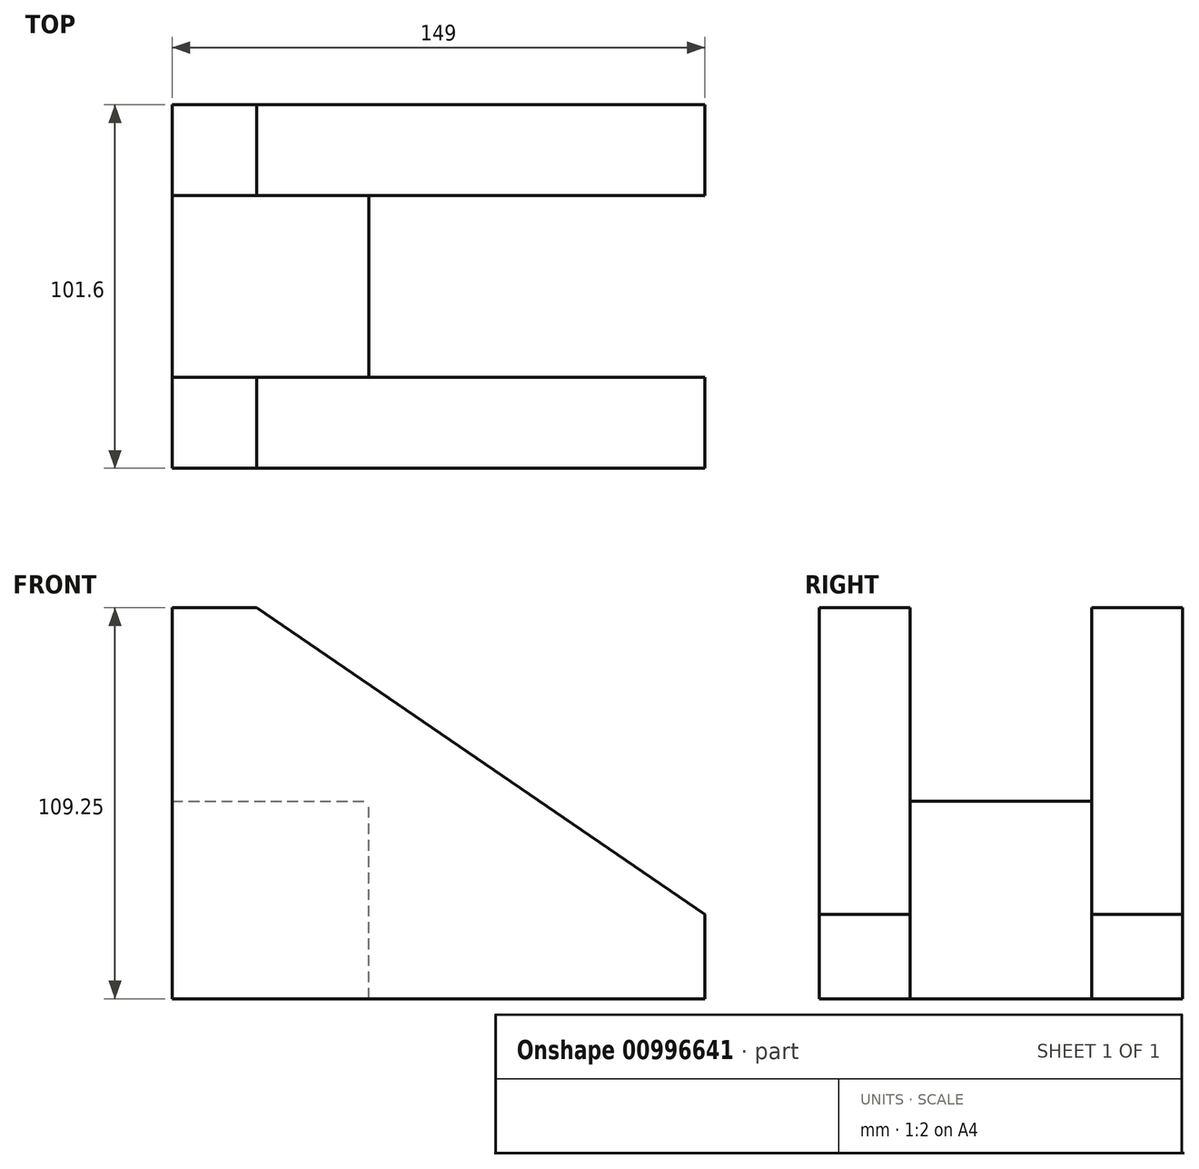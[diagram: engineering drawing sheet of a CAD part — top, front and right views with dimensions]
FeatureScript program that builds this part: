
annotation { "Feature Type Name" : "Feature", "Feature Type Description" : "" }
export const myFeature = defineFeature(function(context is Context, id is Id, definition is map)
    precondition{}
    {
        {
            var Q0;
            Q0=qCreatedBy(makeId("Front.planeOp"),FACE);
            var sketch = newSketch(context, id + "F0", { "sketchPlane" : qUnion([Q0])});
            skLineSegment(sketch, "E0", {"start": v(-68.4, -55.17) * mm, "end": v(80.59, -55.17) * mm});
            skLineSegment(sketch, "E1", {"start": v(80.59, -55.17) * mm, "end": v(80.59, -31.64) * mm});
            skLineSegment(sketch, "E2", {"start": v(80.59, -31.64) * mm, "end": v(-44.81, 54.08) * mm});
            skLineSegment(sketch, "E3", {"start": v(-44.81, 54.08) * mm, "end": v(-68.4, 54.08) * mm});
            skLineSegment(sketch, "E4", {"start": v(-68.4, 54.08) * mm, "end": v(-68.4, -55.17) * mm});
            skSolve(sketch);
        }
        {
            var Q0;
            Q0=makeQuery(id+"F0.imprint","IMPRINT",FACE,{"disambiguationData":[TD([[makeQuery(id+"F0.imprint","IMPRINT",EDGE,{"derivedFrom":sQuery(id+"F0.wireOp",EDGE,"E0")}),1.0]])]});
            extrude(context, id + "F1", {"entities" : qUnion([Q0]), "depth" : 25.4 * mm, "offsetDistance" : 25.4 * mm});
        }
        {
            var Q0;
            Q0=qCreatedBy(makeId("Front.planeOp"),FACE);
            cPlane(context, id + "F2", {"entities" : qUnion([Q0]), "cplaneType" : CPlaneType.OFFSET, "offset" : 25.4 * mm, "oppositeDirection" : true, "width" : 152.4 * mm, "height" : 152.4 * mm});
        }
        {
            var Q0;
            Q0=makeQuery(id+"F1.opExtrude","SWEPT_BODY",BODY,{"disambiguationData":[OSD([sQuery(id+"F0.wireOp",EDGE,"E0"),sQuery(id+"F0.wireOp",EDGE,"E1"),sQuery(id+"F0.wireOp",EDGE,"E2"),sQuery(id+"F0.wireOp",EDGE,"E3"),sQuery(id+"F0.wireOp",EDGE,"E4")])]});
            var Q1;
            Q1=qCreatedBy(id+"F2.planeOp",FACE);
            mirror(context, id + "F3", {"entities" : qUnion([Q0]), "mirrorPlane" : qUnion([Q1])});
        }
        {
            var Q0;
            Q0=makeQuery(id+"F1.opExtrude","CAP_FACE",FACE,{"disambiguationData":[OSD([sQuery(id+"F0.wireOp",EDGE,"E0"),sQuery(id+"F0.wireOp",EDGE,"E1"),sQuery(id+"F0.wireOp",EDGE,"E2"),sQuery(id+"F0.wireOp",EDGE,"E3"),sQuery(id+"F0.wireOp",EDGE,"E4")])],"isStart":true});
            var sketch = newSketch(context, id + "F4", { "sketchPlane" : qUnion([Q0])});
            skLineSegment(sketch, "E5.bottom", {"start": v(68.4, -55.17) * mm, "end": v(13.39, -55.17) * mm});
            skLineSegment(sketch, "E5.top", {"start": v(68.4, 0) * mm, "end": v(13.39, 0) * mm});
            skLineSegment(sketch, "E5.left", {"start": v(68.4, -55.17) * mm, "end": v(68.4, 0) * mm});
            skLineSegment(sketch, "E5.right", {"start": v(13.39, -55.17) * mm, "end": v(13.39, 0) * mm});
            skSolve(sketch);
        }
        {
            var Q0;
            Q0=makeQuery(id+"F4.imprint","IMPRINT",FACE,{"disambiguationData":[TD([[makeQuery(id+"F4.imprint","IMPRINT",EDGE,{"derivedFrom":sQuery(id+"F4.wireOp",EDGE,"E5.bottom")}),-1.0]])]});
            var Q1;
            Q1=makeQuery(id+"F3.opPattern","COPY",BODY,{"derivedFrom":makeQuery(id+"F1.opExtrude","SWEPT_BODY",BODY,{"disambiguationData":[OSD([sQuery(id+"F0.wireOp",EDGE,"E0"),sQuery(id+"F0.wireOp",EDGE,"E1"),sQuery(id+"F0.wireOp",EDGE,"E2"),sQuery(id+"F0.wireOp",EDGE,"E3"),sQuery(id+"F0.wireOp",EDGE,"E4")])]}),"instanceName":"1"});
            extrude(context, id + "F5", {"entities" : qUnion([Q0]), "endBound" : BoundingType.UP_TO_BODY, "depth" : 25.4 * mm, "endBoundEntityBody" : qUnion([Q1]), "offsetDistance" : 25.4 * mm});
        }
    });
